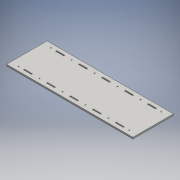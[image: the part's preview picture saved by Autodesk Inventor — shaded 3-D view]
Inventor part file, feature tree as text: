
AUTODESK INVENTOR PART (.ipt)
format: ipt  version: 2016 (Build 200138000, 138)  size: 182,784 bytes
history: native  units: mm
features: extrude x2, sketch x2, other x1
ambient origin geometry x8: Origin, YZ Plane, XZ Plane, XY Plane, X Axis, Y Axis, Z Axis, Center Point
bodies: Body1 (feature_tree)
feature tree (5):
  other  "Sólido1"
  extrude  "Extrusión1"  Depth=3.6mm
  extrude  "Extrusión2"  Depth=6.0mm TaperAngle=0.0deg
  sketch  "Boceto1"  dims[d0=3.6mm d1=3.6mm d2=3.6mm d3=3.6mm d4=3.6mm d5=3.6mm d7=3.6mm d8=3.6mm d9=3.6mm d11=3.6mm]
  sketch  "Boceto2"  dims[d12=3.6mm d13=6.0mm d14=0.0mm d15=3.6mm d16=3.6mm d17=3.6mm d18=3.6mm d19=3.6mm d20=3.6mm d22=3.6mm d23=3.6mm d24=3.6mm d26=3.6mm d27=3.6mm d28=6.0mm d29=0.0mm]
